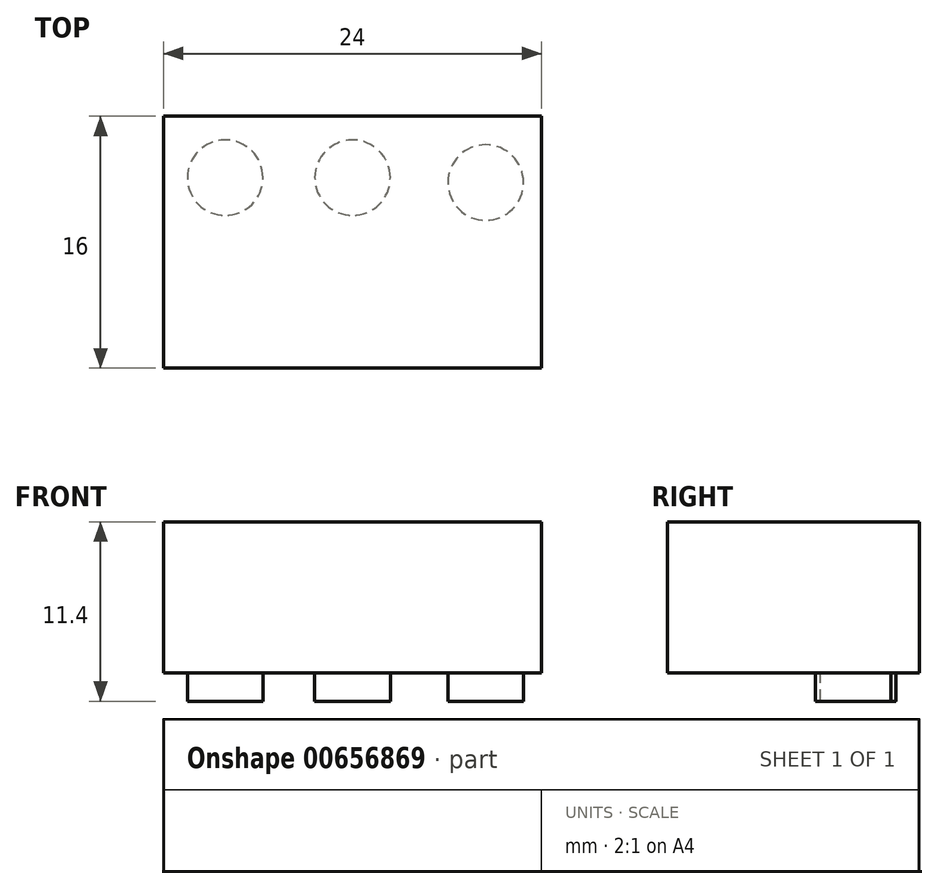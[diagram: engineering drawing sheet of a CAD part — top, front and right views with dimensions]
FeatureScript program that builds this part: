
annotation { "Feature Type Name" : "Feature", "Feature Type Description" : "" }
export const myFeature = defineFeature(function(context is Context, id is Id, definition is map)
    precondition{}
    {
        {
            var Q0;
            Q0=qCreatedBy(makeId("Top.planeOp"),FACE);
            var sketch = newSketch(context, id + "F0", { "sketchPlane" : qUnion([Q0])});
            skLineSegment(sketch, "E0.bottom", {"start": v(0, 0) * mm, "end": v(-24, 0) * mm});
            skLineSegment(sketch, "E0.top", {"start": v(0, 16) * mm, "end": v(-24, 16) * mm});
            skLineSegment(sketch, "E0.left", {"start": v(0, 0) * mm, "end": v(0, 16) * mm});
            skLineSegment(sketch, "E0.right", {"start": v(-24, 0) * mm, "end": v(-24, 16) * mm});
            skSolve(sketch);
        }
        {
            var Q0;
            Q0=makeQuery(id+"F0.imprint","IMPRINT",FACE,{"disambiguationData":[TD([[makeQuery(id+"F0.imprint","IMPRINT",EDGE,{"derivedFrom":sQuery(id+"F0.wireOp",EDGE,"E0.bottom")}),-1.0]])]});
            extrude(context, id + "F1", {"entities" : qUnion([Q0]), "depth" : 9.6 * mm, "offsetDistance" : 25.4 * mm});
        }
        {
            var Q0;
            Q0=qCreatedBy(makeId("Top.planeOp"),FACE);
            var sketch = newSketch(context, id + "F2", { "sketchPlane" : qUnion([Q0])});
            skLineSegment(sketch, "E1", {"start": v(-23.98, 8.16) * mm, "end": v(0, 8.16) * mm, "construction": true});
            skLineSegment(sketch, "E2", {"start": v(-16, 17.28) * mm, "end": v(-16, 0) * mm, "construction": true});
            skLineSegment(sketch, "E3", {"start": v(-8, 17.2) * mm, "end": v(-8, 0) * mm, "construction": true});
            skLineSegment(sketch, "E4", {"start": v(-24.18, 16.04) * mm, "end": v(-16, 8.16) * mm, "construction": true});
            skLineSegment(sketch, "E5", {"start": v(-16, 8.16) * mm, "end": v(-8, 16.04) * mm, "construction": true});
            skLineSegment(sketch, "E6", {"start": v(-8, 16.04) * mm, "end": v(0, 8.16) * mm, "construction": true});
            skCircle(sketch, "E7", {"center": v(-20.1, 12.1) * mm, "radius": 2.4 * mm});
            skCircle(sketch, "E8", {"center": v(-12, 12.1) * mm, "radius": 2.4 * mm});
            skCircle(sketch, "E9", {"center": v(-3.54, 11.8) * mm, "radius": 2.4 * mm});
            skCircle(sketch, "E10.MirrorC", {"center": v(-20.1, 4.22) * mm, "radius": 2.4 * mm});
            skCircle(sketch, "E11.MirrorC", {"center": v(-12, 4.22) * mm, "radius": 2.4 * mm});
            skCircle(sketch, "E12.MirrorC", {"center": v(-3.54, 4.52) * mm, "radius": 2.4 * mm});
            skSolve(sketch);
        }
        {
            var Q0;
            Q0=makeQuery(id+"F2.imprint","IMPRINT",FACE,{"disambiguationData":[TD([[makeQuery(id+"F2.imprint","IMPRINT",EDGE,{"derivedFrom":sQuery(id+"F2.wireOp",EDGE,"E7")}),1.0]])]});
            var Q1;
            Q1=makeQuery(id+"F2.imprint","IMPRINT",FACE,{"disambiguationData":[TD([[makeQuery(id+"F2.imprint","IMPRINT",EDGE,{"derivedFrom":sQuery(id+"F2.wireOp",EDGE,"E8")}),1.0]])]});
            var Q2;
            Q2=makeQuery(id+"F2.imprint","IMPRINT",FACE,{"disambiguationData":[TD([[makeQuery(id+"F2.imprint","IMPRINT",EDGE,{"derivedFrom":sQuery(id+"F2.wireOp",EDGE,"E9")}),1.0]])]});
            var Q3;
            Q3=makeQuery(id+"F2.imprint","IMPRINT",FACE,{"disambiguationData":[TD([[makeQuery(id+"F2.imprint","IMPRINT",EDGE,{"derivedFrom":sQuery(id+"F2.wireOp",EDGE,"E12.MirrorC")}),-1.0]])]});
            var Q4;
            Q4=makeQuery(id+"F2.imprint","IMPRINT",FACE,{"disambiguationData":[TD([[makeQuery(id+"F2.imprint","IMPRINT",EDGE,{"derivedFrom":sQuery(id+"F2.wireOp",EDGE,"E11.MirrorC")}),-1.0]])]});
            var Q5;
            Q5=makeQuery(id+"F2.imprint","IMPRINT",FACE,{"disambiguationData":[TD([[makeQuery(id+"F2.imprint","IMPRINT",EDGE,{"derivedFrom":sQuery(id+"F2.wireOp",EDGE,"E10.MirrorC")}),-1.0]])]});
            extrude(context, id + "F3", {"entities" : qUnion([Q0, Q1, Q2, Q3, Q4, Q5]), "operationType" : NewBodyOperationType.ADD, "oppositeDirection" : true, "depth" : 1.8 * mm, "offsetDistance" : 25.4 * mm});
        }
    });
